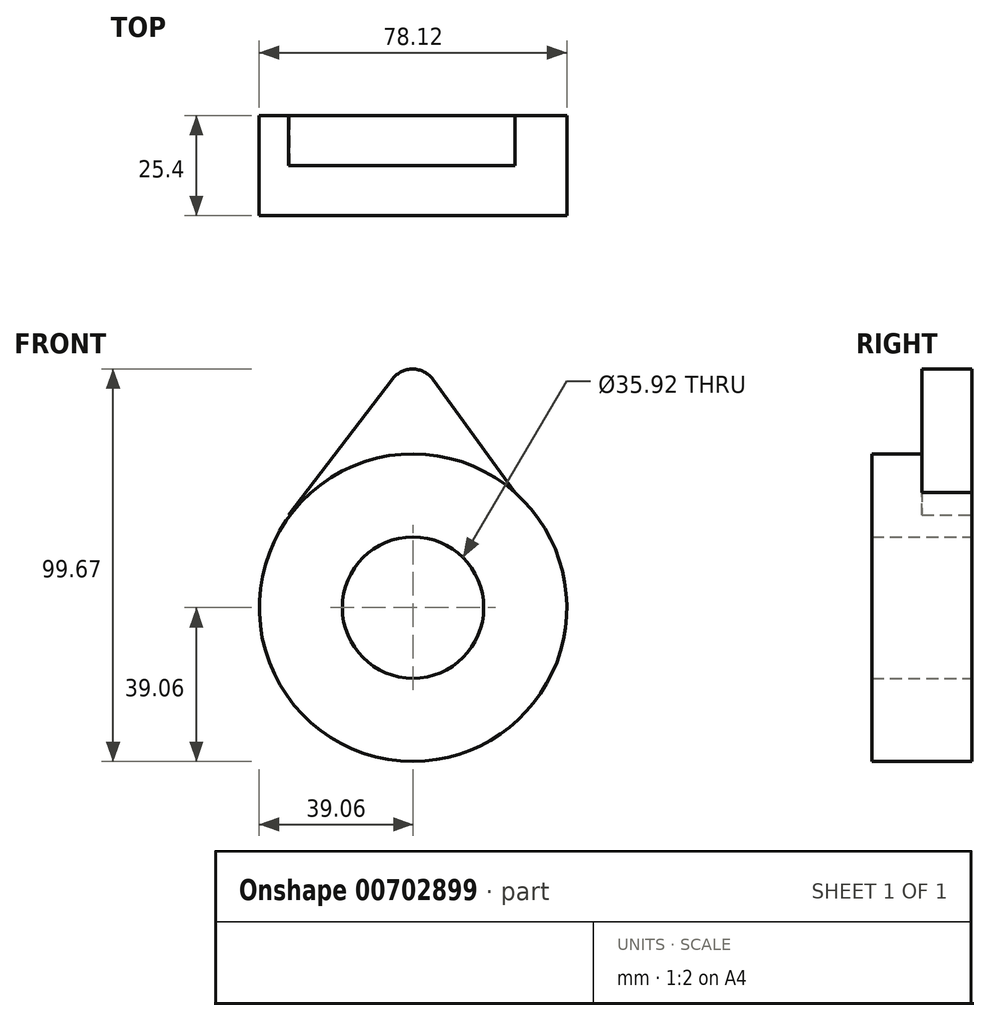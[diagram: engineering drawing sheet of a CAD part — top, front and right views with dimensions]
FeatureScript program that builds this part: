
annotation { "Feature Type Name" : "Feature", "Feature Type Description" : "" }
export const myFeature = defineFeature(function(context is Context, id is Id, definition is map)
    precondition{}
    {
        {
            var Q0;
            Q0=qCreatedBy(makeId("Front.planeOp"),FACE);
            var sketch = newSketch(context, id + "F0", { "sketchPlane" : qUnion([Q0])});
            skCircle(sketch, "E0", {"center": v(0, 0) * mm, "radius": 39.06 * mm});
            skCircle(sketch, "E1", {"center": v(0, 0) * mm, "radius": 17.96 * mm});
            skSolve(sketch);
        }
        {
            var Q0;
            Q0 = qSketchRegion(id + "F0", true);
            extrude(context, id + "F1", {"entities" : qUnion([Q0]), "depth" : 25.4 * mm, "offsetDistance" : 25.4 * mm});
        }
        {
            var Q0;
            Q0=qCreatedBy(makeId("Front.planeOp"),FACE);
            var sketch = newSketch(context, id + "F2", { "sketchPlane" : qUnion([Q0])});
            skLineSegment(sketch, "E2", {"start": v(-31.56, 23.49) * mm, "end": v(-5.17, 58.1) * mm});
            skLineSegment(sketch, "E3", {"start": v(5.01, 58) * mm, "end": v(30.1, 23.49) * mm});
            skLineSegment(sketch, "E4", {"start": v(30.1, 23.49) * mm, "end": v(-31.56, 23.49) * mm});
            skPoint(sketch, "E5.visualSharp", {"position": v(0, 64.89) * mm});
            skArc(sketch, "E5.filletArc", {"start": v(5.01, 58) * mm, "mid": v(-0.05, 60.6) * mm, "end": v(-5.17, 58.1) * mm});
            skSolve(sketch);
        }
        {
            var Q0;
            Q0 = qSketchRegion(id + "F2", true);
            extrude(context, id + "F3", {"entities" : qUnion([Q0]), "operationType" : NewBodyOperationType.ADD, "depth" : 12.7 * mm, "offsetDistance" : 25.4 * mm});
        }
    });
